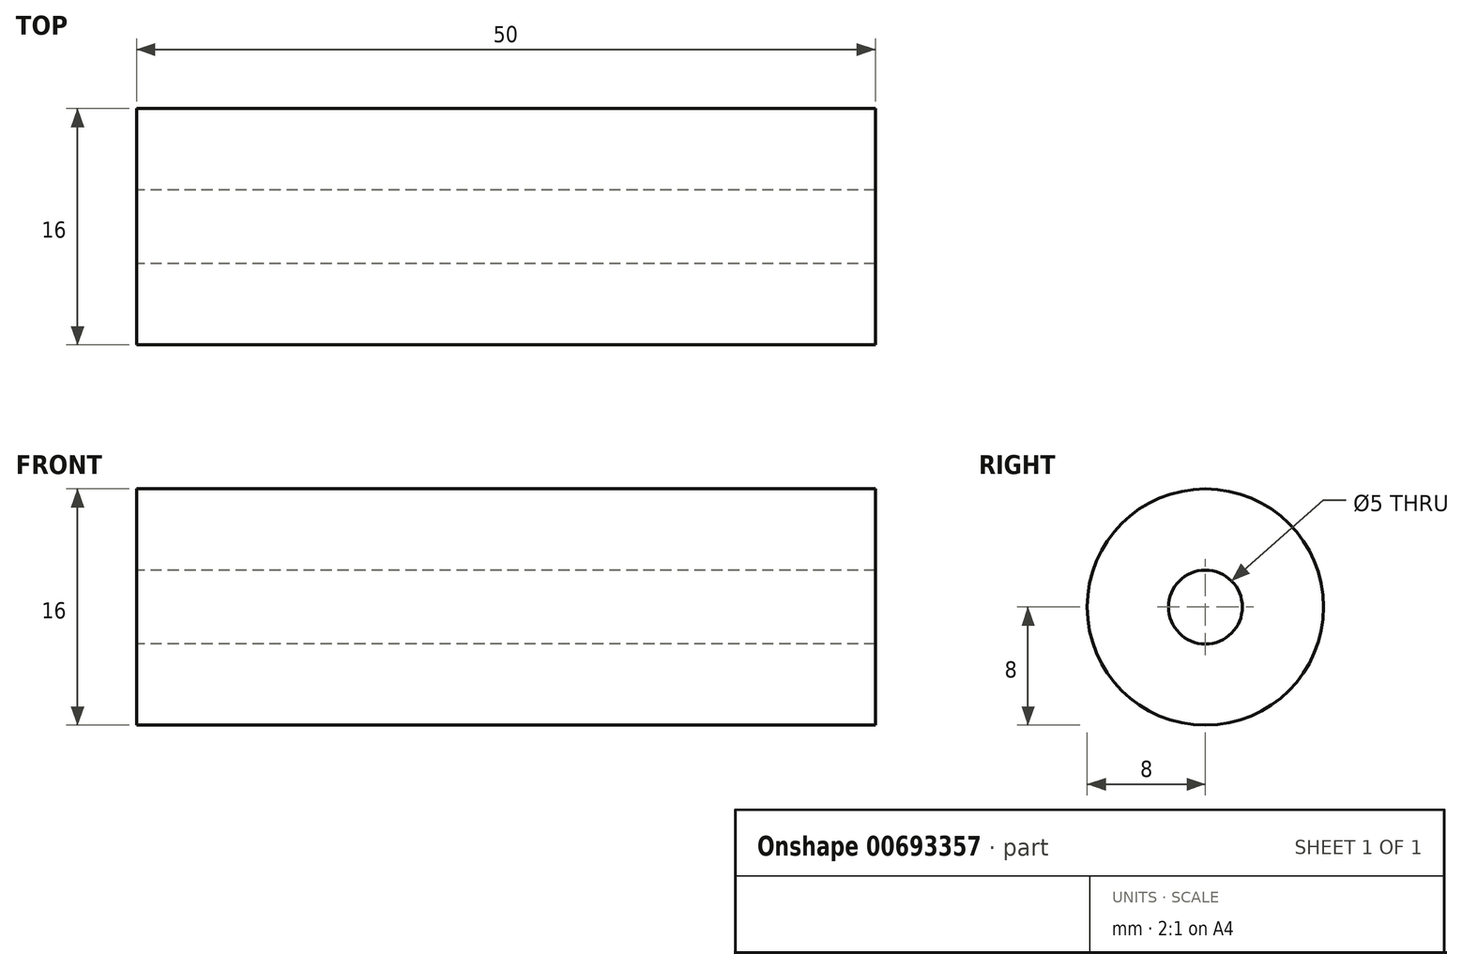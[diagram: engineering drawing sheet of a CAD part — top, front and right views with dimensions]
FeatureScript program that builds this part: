
annotation { "Feature Type Name" : "Feature", "Feature Type Description" : "" }
export const myFeature = defineFeature(function(context is Context, id is Id, definition is map)
    precondition{}
    {
        {
            var Q0;
            Q0=qCreatedBy(makeId("Right.planeOp"),FACE);
            var sketch = newSketch(context, id + "F0", { "sketchPlane" : qUnion([Q0])});
            skCircle(sketch, "E0", {"center": v(0, 0) * mm, "radius": 2.5 * mm});
            skCircle(sketch, "E1", {"center": v(0, 0) * mm, "radius": 8 * mm});
            skSolve(sketch);
        }
        {
            var Q0;
            Q0=makeQuery(id+"F0.imprint","IMPRINT",FACE,{"disambiguationData":[TD([[makeQuery(id+"F0.imprint","IMPRINT",EDGE,{"derivedFrom":sQuery(id+"F0.wireOp",EDGE,"E0")}),-1.0]])]});
            extrude(context, id + "F1", {"entities" : qUnion([Q0]), "depth" : 50 * mm, "offsetDistance" : 25 * mm, "symmetric" : true});
        }
    });
